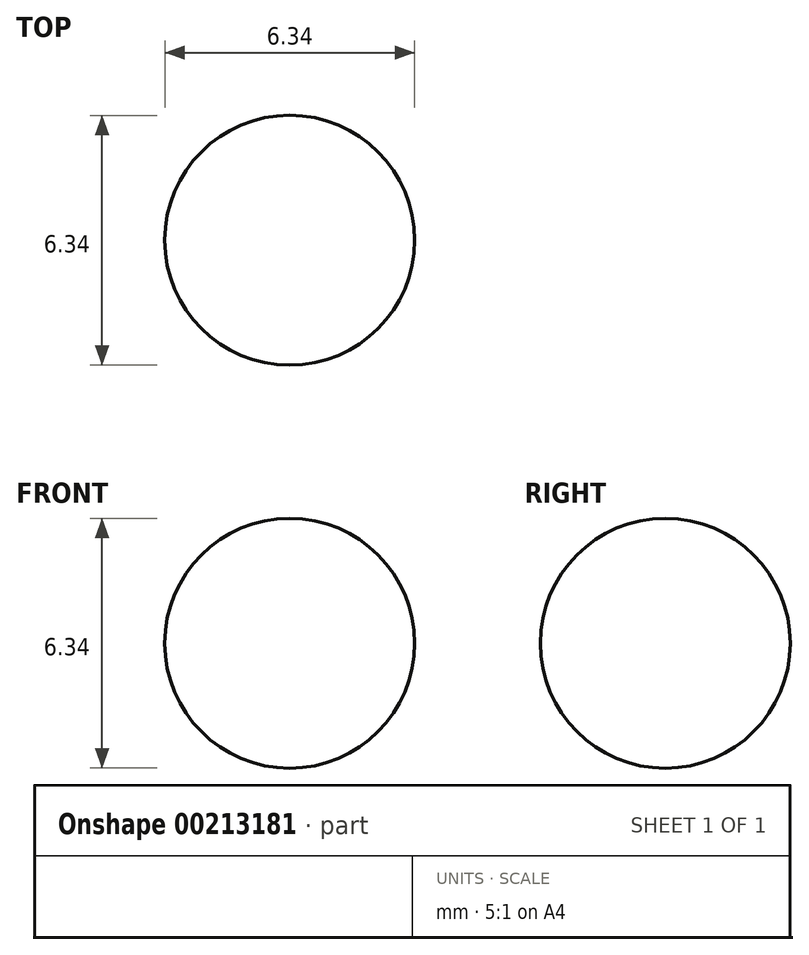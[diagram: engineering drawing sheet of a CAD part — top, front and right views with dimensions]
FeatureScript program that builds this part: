
annotation { "Feature Type Name" : "Feature", "Feature Type Description" : "" }
export const myFeature = defineFeature(function(context is Context, id is Id, definition is map)
    precondition{}
    {
        {
            var Q0;
            Q0=qCreatedBy(makeId("Front.planeOp"),FACE);
            var sketch = newSketch(context, id + "F0", { "sketchPlane" : qUnion([Q0])});
            skArc(sketch, "E0", {"start": v(3.18, 0) * mm, "mid": v(0, 3.18) * mm, "end": v(-3.18, 0) * mm});
            skLineSegment(sketch, "E1", {"start": v(-3.18, 0) * mm, "end": v(3.18, 0) * mm});
            skSolve(sketch);
        }
        {
            var Q0;
            Q0=makeQuery(id+"F0.imprint","IMPRINT",FACE,{"disambiguationData":[TD([[makeQuery(id+"F0.imprint","IMPRINT",EDGE,{"derivedFrom":sQuery(id+"F0.wireOp",EDGE,"E0")}),1.0]])]});
            var Q1;
            Q1=sQuery(id+"F0.wireOp",EDGE,"E1");
            revolve(context, id + "F1", {"entities" : qUnion([Q0]), "axis" : qUnion([Q1]), "revolveType" : RevolveType.FULL});
        }
    });
